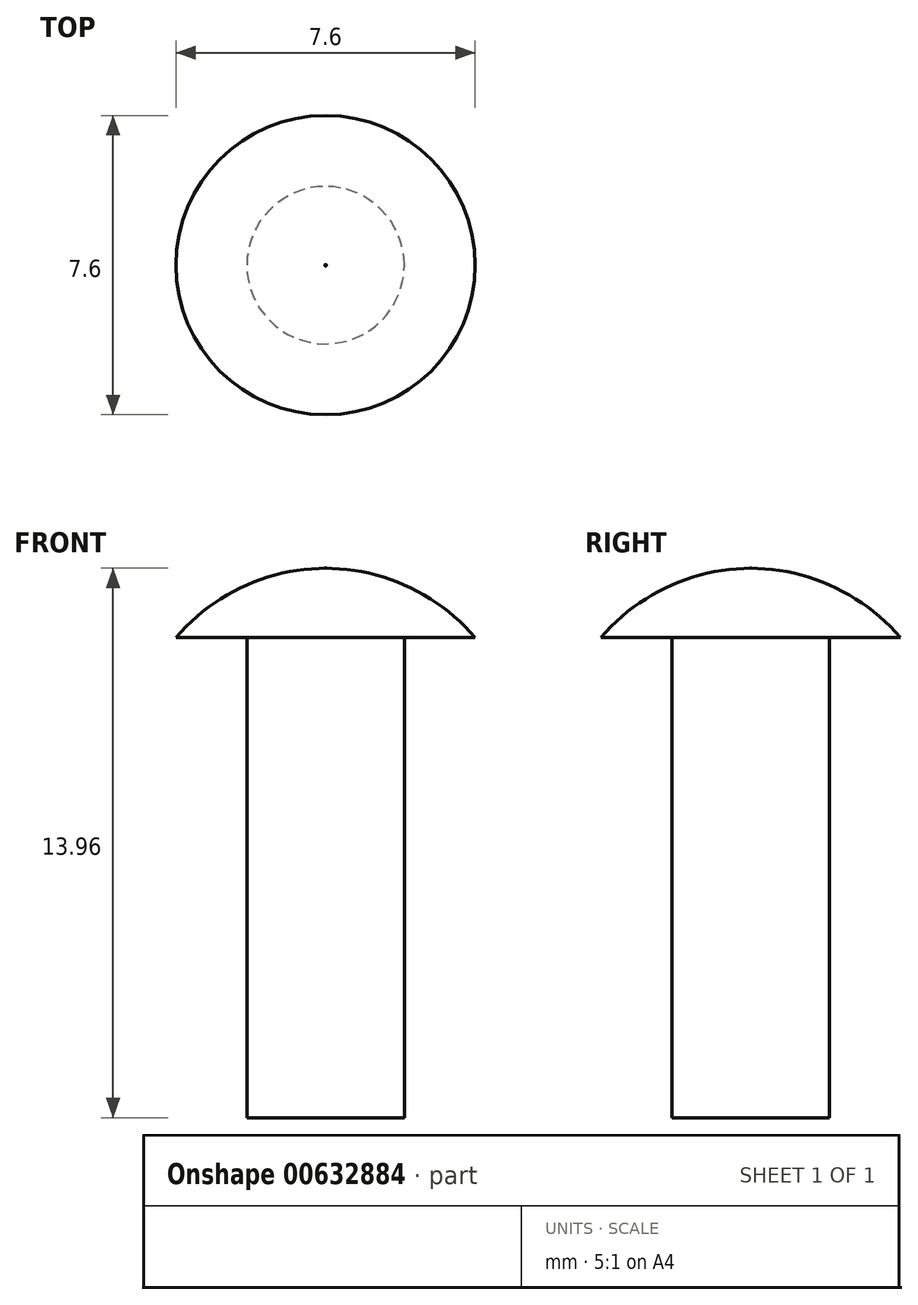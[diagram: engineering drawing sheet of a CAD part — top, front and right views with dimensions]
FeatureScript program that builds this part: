
annotation { "Feature Type Name" : "Feature", "Feature Type Description" : "" }
export const myFeature = defineFeature(function(context is Context, id is Id, definition is map)
    precondition{}
    {
        {
            var Q0;
            Q0=qCreatedBy(makeId("Front.planeOp"),FACE);
            var sketch = newSketch(context, id + "F0", { "sketchPlane" : qUnion([Q0])});
            skLineSegment(sketch, "E0", {"start": v(0, 18.64) * mm, "end": v(-3.8, 18.64) * mm});
            skArc(sketch, "E1", {"start": v(0, 20.4) * mm, "mid": v(-2.1, 19.93) * mm, "end": v(-3.8, 18.64) * mm});
            skLineSegment(sketch, "E2", {"start": v(0, 20.4) * mm, "end": v(0, 18.64) * mm});
            skLineSegment(sketch, "E3", {"start": v(-2, 18.64) * mm, "end": v(-2, 6.44) * mm});
            skLineSegment(sketch, "E4", {"start": v(-2, 6.44) * mm, "end": v(0, 6.44) * mm});
            skLineSegment(sketch, "E5", {"start": v(0, 6.44) * mm, "end": v(0, 18.64) * mm});
            skSolve(sketch);
        }
        {
            var Q0;
            {var subQ3=sQuery(id+"F0.wireOp",EDGE,"E1");Q0=makeQuery(id+"F0.imprint","IMPRINT",FACE,{"disambiguationData":[TD([[makeQuery(id+"F0.imprint","IMPRINT",EDGE,{"derivedFrom":subQ3}),1.0]])]});}
            var Q1;
            {var subQ2=sQuery(id+"F0.wireOp",EDGE,"E3");Q1=makeQuery(id+"F0.imprint","IMPRINT",FACE,{"disambiguationData":[TD([[makeQuery(id+"F0.imprint","IMPRINT",EDGE,{"derivedFrom":subQ2}),1.0]])]});}
            var Q2;
            Q2=sQuery(id+"F0.wireOp",EDGE,"E5");
            revolve(context, id + "F1", {"entities" : qUnion([Q0, Q1]), "axis" : qUnion([Q2]), "revolveType" : RevolveType.FULL});
        }
    });
